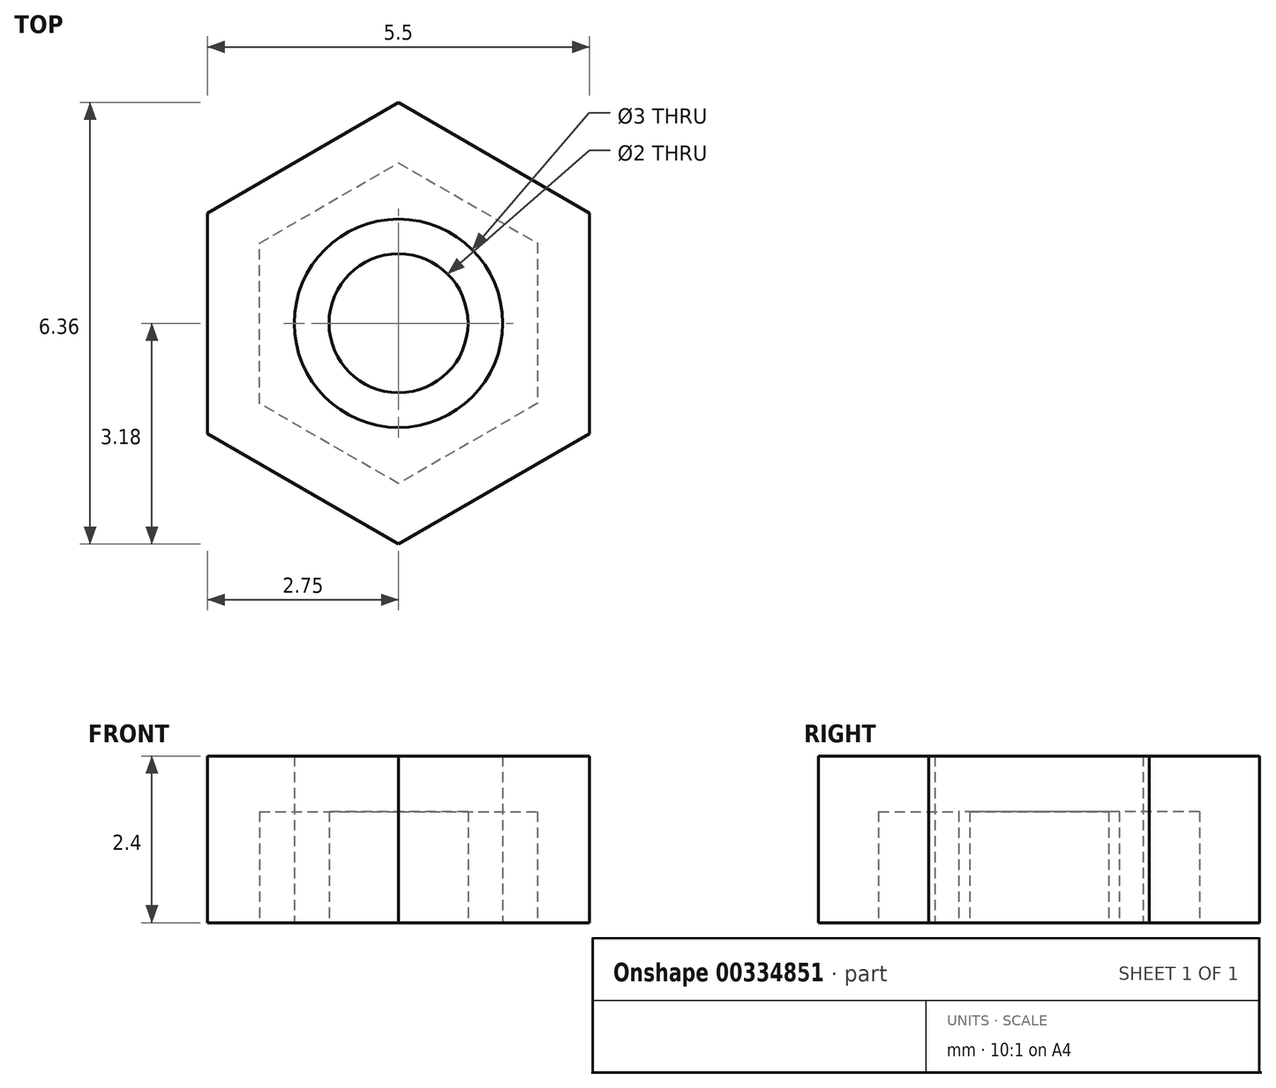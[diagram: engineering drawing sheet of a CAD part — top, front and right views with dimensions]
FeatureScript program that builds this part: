
annotation { "Feature Type Name" : "Feature", "Feature Type Description" : "" }
export const myFeature = defineFeature(function(context is Context, id is Id, definition is map)
    precondition{}
    {
        {
            var Q0;
            Q0=qCreatedBy(makeId("Top.planeOp"),FACE);
            var sketch = newSketch(context, id + "F0", { "sketchPlane" : qUnion([Q0])});
            skCircle(sketch, "E0.cCircle", {"center": v(0, 0) * mm, "radius": 2 * mm, "construction": true});
            skLineSegment(sketch, "E0.0", {"start": v(2, 1.15) * mm, "end": v(2, -1.15) * mm});
            skLineSegment(sketch, "E0.1", {"start": v(2, -1.15) * mm, "end": v(0, -2.3) * mm});
            skLineSegment(sketch, "E0.2", {"start": v(0, -2.3) * mm, "end": v(-2, -1.15) * mm});
            skLineSegment(sketch, "E0.3", {"start": v(-2, -1.15) * mm, "end": v(-2, 1.15) * mm});
            skLineSegment(sketch, "E0.4", {"start": v(-2, 1.15) * mm, "end": v(0, 2.3) * mm});
            skLineSegment(sketch, "E0.5", {"start": v(0, 2.3) * mm, "end": v(2, 1.15) * mm});
            skPoint(sketch, "E0.0.midPoint", {"position": v(2, 0) * mm});
            skCircle(sketch, "E1", {"center": v(0, 0) * mm, "radius": 1 * mm});
            skSolve(sketch);
        }
        {
            var Q0;
            Q0 = qSketchRegion(id + "F0", true);
            extrude(context, id + "F1", {"entities" : qUnion([Q0]), "depth" : 1.6 * mm, "offsetDistance" : 25 * mm});
        }
        {
            var Q0;
            Q0=qCreatedBy(makeId("Top.planeOp"),FACE);
            var sketch = newSketch(context, id + "F2", { "sketchPlane" : qUnion([Q0])});
            skCircle(sketch, "E2.cCircle", {"center": v(0, 0) * mm, "radius": 2.75 * mm, "construction": true});
            skLineSegment(sketch, "E2.0", {"start": v(2.75, 1.59) * mm, "end": v(2.75, -1.59) * mm});
            skLineSegment(sketch, "E2.1", {"start": v(2.75, -1.59) * mm, "end": v(0, -3.18) * mm});
            skLineSegment(sketch, "E2.2", {"start": v(0, -3.18) * mm, "end": v(-2.75, -1.59) * mm});
            skLineSegment(sketch, "E2.3", {"start": v(-2.75, -1.59) * mm, "end": v(-2.75, 1.59) * mm});
            skLineSegment(sketch, "E2.4", {"start": v(-2.75, 1.59) * mm, "end": v(0, 3.18) * mm});
            skLineSegment(sketch, "E2.5", {"start": v(0, 3.18) * mm, "end": v(2.75, 1.59) * mm});
            skPoint(sketch, "E2.0.midPoint", {"position": v(2.75, 0) * mm});
            skCircle(sketch, "E3", {"center": v(0, 0) * mm, "radius": 1.5 * mm});
            skSolve(sketch);
        }
        {
            var Q0;
            Q0 = qSketchRegion(id + "F2", true);
            extrude(context, id + "F3", {"entities" : qUnion([Q0]), "depth" : 2.4 * mm, "offsetDistance" : 25 * mm});
        }
    });
